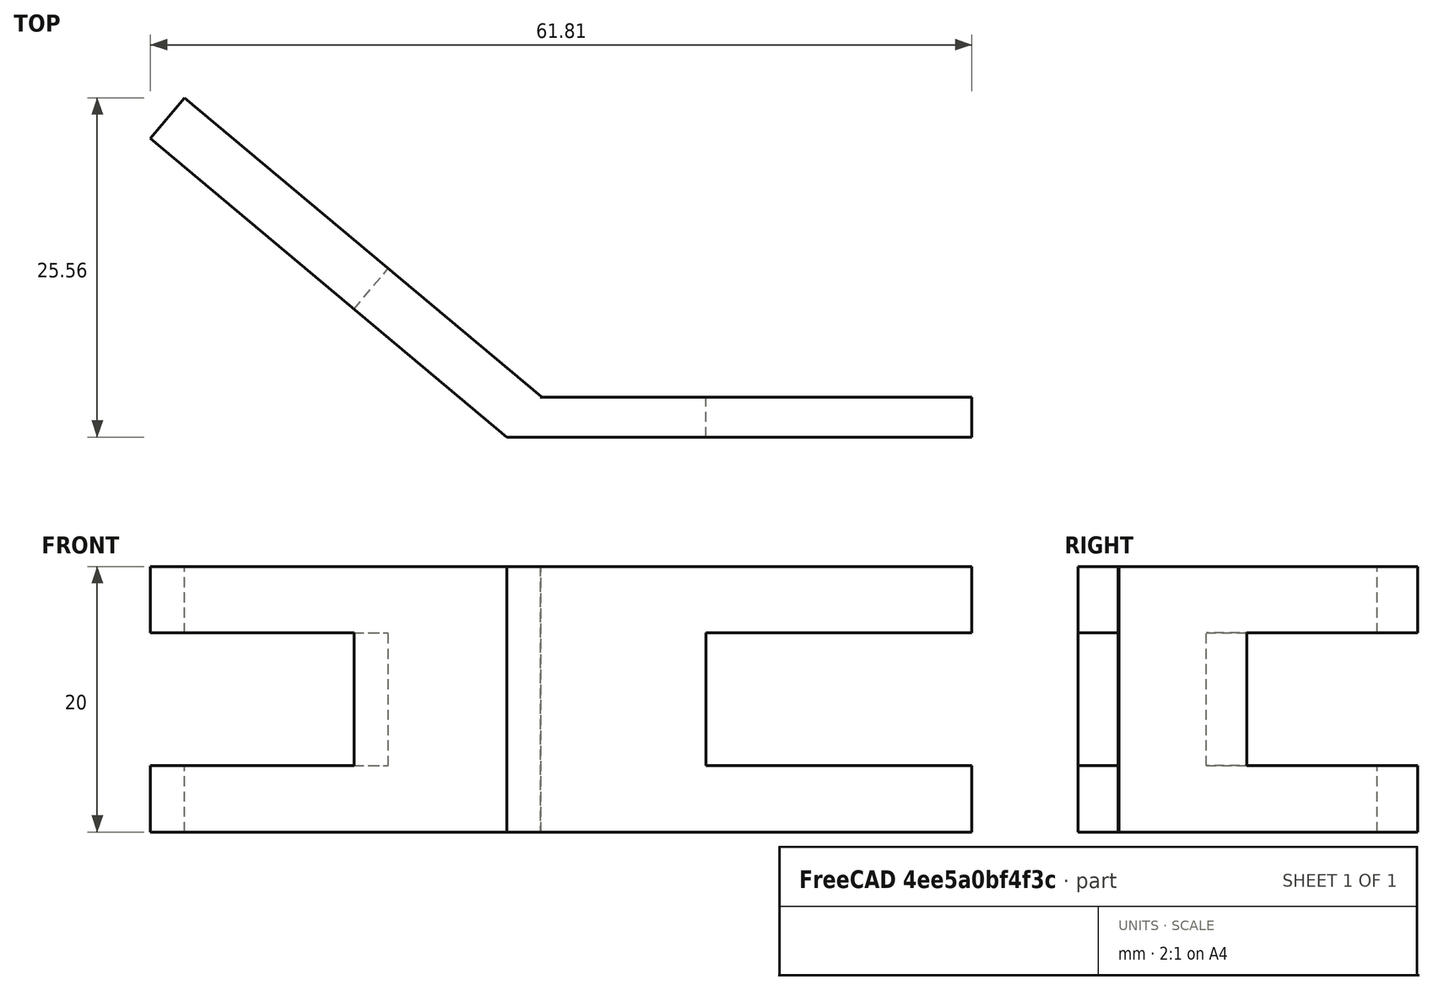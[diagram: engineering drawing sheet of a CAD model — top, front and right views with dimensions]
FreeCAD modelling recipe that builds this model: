
FCSTD DOCUMENT
Label: j-support_v0
objects: Part::Box×2, Part::Mirroring×2, Part::Cut×2, Part::Fuse×1
note: 7 computed .brp shape members not serialized (recipe doc carries the construction recipe); baked Part::Feature solids carry a one-line shape summary decoded from their .brp

FEATURE [Part::Box] Box001
  Height = 20
  Length = 35
  Width = 3
FEATURE [Part::Mirroring] Part__Mirroring  label="Box001001 (Mirror #1)"
  Base = (0,0,0)
  Normal = (1,0,0)
  Placement = pos=(0,0,0) rot=(0,0,-1;0.698131rad)
FEATURE [Part::Box] Box
  Height = 10
  Length = 25
  Placement = pos=(15,-3,5) rot=(0,0,1;0rad)
  Width = 10
FEATURE [Part::Mirroring] Part__Mirroring001  label="Box (Mirror #2)"
  Base = (0,0,0)
  Normal = (1,0,0)
  Placement = pos=(0,0,0) rot=(0,0,-1;0.698131rad)
  Source = -> Box
FEATURE [Part::Fuse] Fusion
  Base = -> Box001
  Tool = -> Part__Mirroring
FEATURE [Part::Cut] Cut
  Base = -> Fusion
  Tool = -> Box
FEATURE [Part::Cut] Cut001
  Base = -> Cut
  Tool = -> Part__Mirroring001
